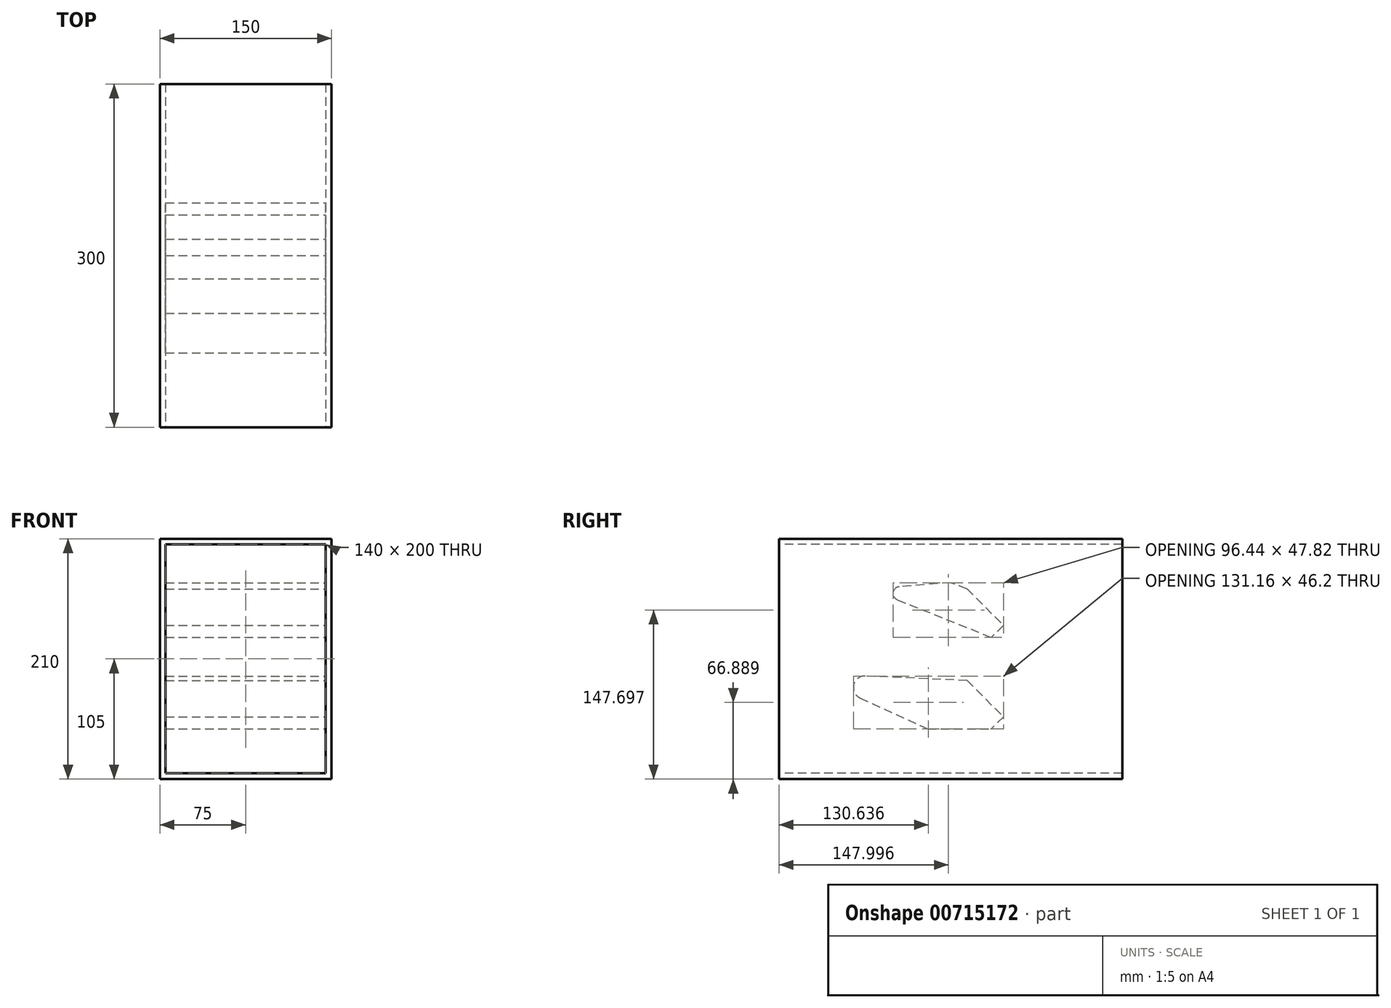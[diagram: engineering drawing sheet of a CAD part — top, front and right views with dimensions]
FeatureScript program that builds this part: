
annotation { "Feature Type Name" : "Feature", "Feature Type Description" : "" }
export const myFeature = defineFeature(function(context is Context, id is Id, definition is map)
    precondition{}
    {
        {
            var Q0;
            Q0=qCreatedBy(makeId("Front.planeOp"),FACE);
            var sketch = newSketch(context, id + "F0", { "sketchPlane" : qUnion([Q0])});
            skLineSegment(sketch, "E0.bottom", {"start": v(-70, 100) * mm, "end": v(70, 100) * mm});
            skLineSegment(sketch, "E0.top", {"start": v(-70, -100) * mm, "end": v(70, -100) * mm});
            skLineSegment(sketch, "E0.left", {"start": v(-70, 100) * mm, "end": v(-70, -100) * mm});
            skLineSegment(sketch, "E0.right", {"start": v(70, 100) * mm, "end": v(70, -100) * mm});
            skLineSegment(sketch, "E1", {"start": v(-152.54, 0) * mm, "end": v(200.9, 0) * mm, "construction": true});
            skLineSegment(sketch, "E2.0", {"start": v(-75, 105) * mm, "end": v(75, 105) * mm});
            skLineSegment(sketch, "E2.1", {"start": v(-75, 105) * mm, "end": v(-75, -105) * mm});
            skLineSegment(sketch, "E2.2", {"start": v(-75, -105) * mm, "end": v(75, -105) * mm});
            skLineSegment(sketch, "E2.3", {"start": v(75, 105) * mm, "end": v(75, -105) * mm});
            skSolve(sketch);
        }
        {
            var Q0;
            Q0 = qSketchRegion(id + "F0", true);
            extrude(context, id + "F1", {"entities" : qUnion([Q0]), "oppositeDirection" : true, "depth" : 300 * mm, "offsetDistance" : 25 * mm});
        }
        {
            var Q0;
            Q0=qCreatedBy(makeId("Right.planeOp"),FACE);
            var sketch = newSketch(context, id + "F2", { "sketchPlane" : qUnion([Q0])});
            skLineSegment(sketch, "E3", {"start": v(-105.65, 0) * mm, "end": v(384.1, 0) * mm, "construction": true});
            skPoint(sketch, "E3.startSnap0", {"position": v(0, 0) * mm});
            skLineSegment(sketch, "E4", {"start": v(150, 141.47) * mm, "end": v(150, -157.63) * mm, "construction": true});
            skPoint(sketch, "E4.startSnap0", {"position": v(150, 100) * mm});
            skLineSegment(sketch, "E5.bottom", {"start": v(164.4, 61.21) * mm, "end": v(196.21, 29.4) * mm});
            skLineSegment(sketch, "E5.top", {"start": v(153.79, 50.6) * mm, "end": v(185.6, 18.79) * mm, "construction": true});
            skLineSegment(sketch, "E5.left", {"start": v(164.4, 61.21) * mm, "end": v(153.79, 50.6) * mm, "construction": true});
            skLineSegment(sketch, "E5.right", {"start": v(196.21, 29.4) * mm, "end": v(185.6, 18.79) * mm});
            skLineSegment(sketch, "E6", {"start": v(159.1, 55.9) * mm, "end": v(190.9, 24.1) * mm, "construction": true});
            skLineSegment(sketch, "E7", {"start": v(180.3, 45.3) * mm, "end": v(169.7, 34.7) * mm, "construction": true});
            skPoint(sketch, "E8", {"position": v(175, 40) * mm});
            skLineSegment(sketch, "E9", {"start": v(175, 40) * mm, "end": v(175, 0) * mm, "construction": true});
            skLineSegment(sketch, "E10.0.1.0", {"start": v(196.21, -50.6) * mm, "end": v(185.6, -61.21) * mm});
            skLineSegment(sketch, "E10.0.1.1", {"start": v(153.79, -29.4) * mm, "end": v(185.6, -61.21) * mm, "construction": true});
            skLineSegment(sketch, "E10.0.1.2", {"start": v(164.4, -18.79) * mm, "end": v(153.79, -29.4) * mm, "construction": true});
            skLineSegment(sketch, "E10.0.1.3", {"start": v(164.4, -18.79) * mm, "end": v(196.21, -50.6) * mm});
            skLineSegment(sketch, "E10.0.1.4", {"start": v(159.1, -24.1) * mm, "end": v(190.9, -55.9) * mm, "construction": true});
            skLineSegment(sketch, "E10.0.1.5", {"start": v(180.3, -34.7) * mm, "end": v(169.7, -45.3) * mm, "construction": true});
            skLineSegment(sketch, "E10.direction1", {"start": v(180.3, 45.3) * mm, "end": v(204.05, 45.3) * mm, "construction": true});
            skLineSegment(sketch, "E10.direction2", {"start": v(180.3, 45.3) * mm, "end": v(180.3, -34.7) * mm, "construction": true});
            skLineSegment(sketch, "E11", {"start": v(164.4, 61.21) * mm, "end": v(150, 66.6) * mm});
            skLineSegment(sketch, "E12", {"start": v(150, 66.6) * mm, "end": v(105.25, 63.18) * mm});
            skLineSegment(sketch, "E13", {"start": v(103.48, 51.63) * mm, "end": v(185.6, 18.79) * mm});
            skPoint(sketch, "E14.visualSharp", {"position": v(79.51, 61.21) * mm});
            skArc(sketch, "E14.filletArc", {"start": v(105.25, 63.18) * mm, "mid": v(99.78, 58.1) * mm, "end": v(103.48, 51.63) * mm});
            skLineSegment(sketch, "E15", {"start": v(164.4, -18.79) * mm, "end": v(75.42, -15) * mm});
            skLineSegment(sketch, "E16", {"start": v(70.83, -34.09) * mm, "end": v(129.9, -61.21) * mm});
            skLineSegment(sketch, "E17", {"start": v(129.9, -61.21) * mm, "end": v(185.6, -61.21) * mm});
            skPoint(sketch, "E18.visualSharp", {"position": v(24.58, -12.85) * mm});
            skArc(sketch, "E18.filletArc", {"start": v(75.42, -15) * mm, "mid": v(65.28, -22.66) * mm, "end": v(70.83, -34.09) * mm});
            skSolve(sketch);
        }
        {
            var Q0;
            Q0=makeQuery(id+"F2.imprint","IMPRINT",FACE,{"disambiguationData":[TD([[makeQuery(id+"F2.imprint","IMPRINT",EDGE,{"derivedFrom":sQuery(id+"F2.wireOp",EDGE,"E5.bottom")}),-1.0]])]});
            var Q1;
            Q1=makeQuery(id+"F1.opExtrude","SWEPT_FACE",FACE,{"disambiguationData":[OSD([sQuery(id+"F0.wireOp",EDGE,"E0.left")])]});
            var Q2;
            Q2=makeQuery(id+"F1.opExtrude","SWEPT_FACE",FACE,{"disambiguationData":[OSD([sQuery(id+"F0.wireOp",EDGE,"E0.right")])]});
            extrude(context, id + "F3", {"entities" : qUnion([Q0]), "endBound" : BoundingType.UP_TO_SURFACE, "oppositeDirection" : true, "depth" : 25 * mm, "endBoundEntityFace" : qUnion([Q1]), "offsetDistance" : 25 * mm, "hasSecondDirection" : true, "secondDirectionBound" : BoundingType.UP_TO_SURFACE, "secondDirectionOppositeDirection" : false, "secondDirectionDepth" : 25 * mm, "secondDirectionBoundEntityFace" : qUnion([Q2])});
        }
        {
            var Q0;
            Q0=makeQuery(id+"F2.imprint","IMPRINT",FACE,{"disambiguationData":[TD([[makeQuery(id+"F2.imprint","IMPRINT",EDGE,{"derivedFrom":sQuery(id+"F2.wireOp",EDGE,"E10.0.1.0")}),-1.0]])]});
            var Q1;
            Q1=makeQuery(id+"F1.opExtrude","SWEPT_FACE",FACE,{"disambiguationData":[OSD([sQuery(id+"F0.wireOp",EDGE,"E0.left")])]});
            var Q2;
            Q2=makeQuery(id+"F1.opExtrude","SWEPT_FACE",FACE,{"disambiguationData":[OSD([sQuery(id+"F0.wireOp",EDGE,"E0.right")])]});
            extrude(context, id + "F4", {"entities" : qUnion([Q0]), "endBound" : BoundingType.UP_TO_SURFACE, "oppositeDirection" : true, "depth" : 25 * mm, "endBoundEntityFace" : qUnion([Q1]), "offsetDistance" : 25 * mm, "hasSecondDirection" : true, "secondDirectionBound" : BoundingType.UP_TO_SURFACE, "secondDirectionOppositeDirection" : false, "secondDirectionDepth" : 25 * mm, "secondDirectionBoundEntityFace" : qUnion([Q2])});
        }
        {
            var Q0;
            Q0=qCreatedBy(makeId("Front.planeOp"),FACE);
            var sketch = newSketch(context, id + "F5", { "sketchPlane" : qUnion([Q0])});
            skLineSegment(sketch, "E19.bottom", {"start": v(-70, 100) * mm, "end": v(70, 100) * mm});
            skLineSegment(sketch, "E19.top", {"start": v(-70, -100) * mm, "end": v(70, -100) * mm});
            skLineSegment(sketch, "E19.left", {"start": v(-70, 100) * mm, "end": v(-70, -100) * mm});
            skLineSegment(sketch, "E19.right", {"start": v(70, 100) * mm, "end": v(70, -100) * mm});
            skSolve(sketch);
        }
        {
            var Q0;
            Q0=makeQuery(id+"F5.imprint","IMPRINT",FACE,{"disambiguationData":[TD([[makeQuery(id+"F5.imprint","IMPRINT",EDGE,{"derivedFrom":sQuery(id+"F5.wireOp",EDGE,"E19.bottom")}),-1.0]])]});
            extrude(context, id + "F6", {"entities" : qUnion([Q0]), "oppositeDirection" : true, "depth" : 300 * mm, "offsetDistance" : 25 * mm});
        }
        {
            var Q0;
            Q0=makeQuery(id+"F3.opExtrude","SWEPT_BODY",BODY,{"disambiguationData":[OSD([sQuery(id+"F2.wireOp",EDGE,"E5.bottom"),sQuery(id+"F2.wireOp",EDGE,"E5.right"),sQuery(id+"F2.wireOp",EDGE,"E11"),sQuery(id+"F2.wireOp",EDGE,"E12"),sQuery(id+"F2.wireOp",EDGE,"E13"),sQuery(id+"F2.wireOp",EDGE,"E14.filletArc")])]});
            var Q1;
            Q1=makeQuery(id+"F4.opExtrude","SWEPT_BODY",BODY,{"disambiguationData":[OSD([sQuery(id+"F2.wireOp",EDGE,"E10.0.1.0"),sQuery(id+"F2.wireOp",EDGE,"E10.0.1.3"),sQuery(id+"F2.wireOp",EDGE,"E15"),sQuery(id+"F2.wireOp",EDGE,"E16"),sQuery(id+"F2.wireOp",EDGE,"E17"),sQuery(id+"F2.wireOp",EDGE,"E18.filletArc")])]});
            var Q2;
            Q2=makeQuery(id+"F6.opExtrude","SWEPT_BODY",BODY,{"disambiguationData":[OSD([sQuery(id+"F5.wireOp",EDGE,"E19.bottom"),sQuery(id+"F5.wireOp",EDGE,"E19.top"),sQuery(id+"F5.wireOp",EDGE,"E19.left"),sQuery(id+"F5.wireOp",EDGE,"E19.right")])]});
            booleanBodies(context, id + "F7", {"operationType" : BooleanOperationType.SUBTRACTION, "tools" : qUnion([Q0, Q1]), "targets" : qUnion([Q2]), "keepTools" : true});
        }
    });
